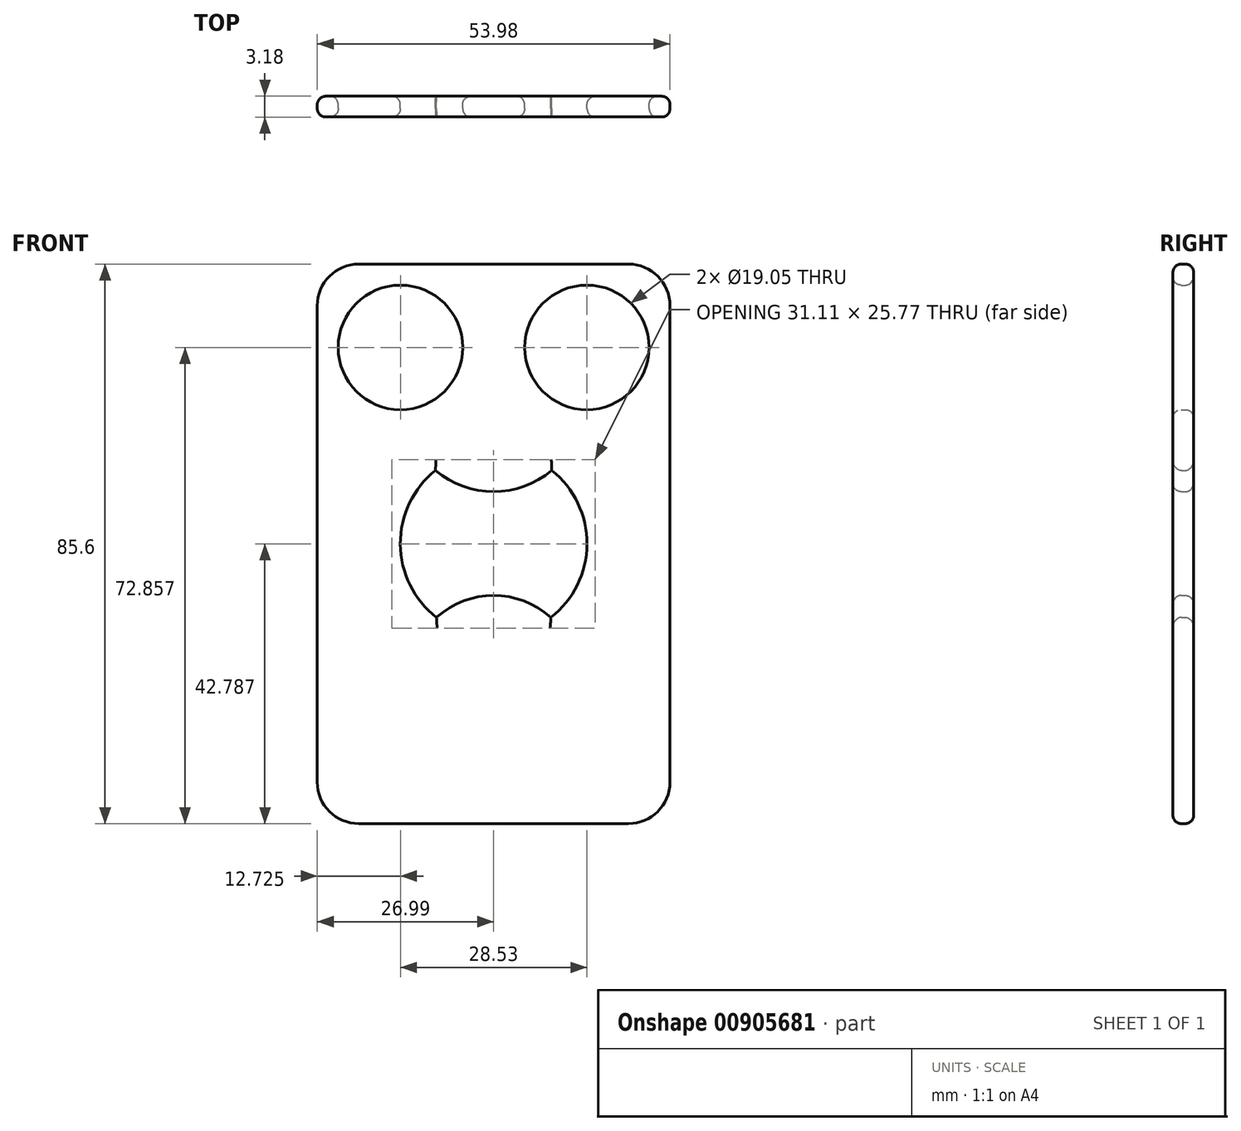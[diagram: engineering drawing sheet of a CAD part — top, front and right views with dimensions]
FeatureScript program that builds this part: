
annotation { "Feature Type Name" : "Feature", "Feature Type Description" : "" }
export const myFeature = defineFeature(function(context is Context, id is Id, definition is map)
    precondition{}
    {
        {
            var Q0;
            Q0=qCreatedBy(makeId("Front.planeOp"),FACE);
            var sketch = newSketch(context, id + "F0", { "sketchPlane" : qUnion([Q0])});
            skLineSegment(sketch, "E0.bottom", {"start": v(-20.64, 42.8) * mm, "end": v(20.64, 42.8) * mm});
            skLineSegment(sketch, "E0.top", {"start": v(-20.64, -42.8) * mm, "end": v(20.64, -42.8) * mm});
            skLineSegment(sketch, "E0.left", {"start": v(-26.99, 36.45) * mm, "end": v(-26.99, -36.45) * mm});
            skLineSegment(sketch, "E0.right", {"start": v(26.99, 36.45) * mm, "end": v(26.99, -36.45) * mm});
            skPoint(sketch, "E0.middle", {"position": v(0, 0) * mm});
            skPoint(sketch, "E1.visualSharp", {"position": v(-26.99, 42.8) * mm});
            skArc(sketch, "E1.filletArc", {"start": v(-20.64, 42.8) * mm, "mid": v(-25.13, 40.94) * mm, "end": v(-26.99, 36.45) * mm});
            skPoint(sketch, "E2.visualSharp", {"position": v(26.99, 42.8) * mm});
            skArc(sketch, "E2.filletArc", {"start": v(26.99, 36.45) * mm, "mid": v(25.13, 40.94) * mm, "end": v(20.64, 42.8) * mm});
            skPoint(sketch, "E3.visualSharp", {"position": v(26.99, -42.8) * mm});
            skArc(sketch, "E3.filletArc", {"start": v(20.64, -42.8) * mm, "mid": v(25.13, -40.94) * mm, "end": v(26.99, -36.45) * mm});
            skPoint(sketch, "E4.visualSharp", {"position": v(-26.99, -42.8) * mm});
            skArc(sketch, "E4.filletArc", {"start": v(-26.99, -36.45) * mm, "mid": v(-25.13, -40.94) * mm, "end": v(-20.64, -42.8) * mm});
            skCircle(sketch, "E5", {"center": v(-14.27, 30.06) * mm, "radius": 9.53 * mm});
            skCircle(sketch, "E6.MirrorC", {"center": v(14.27, 30.06) * mm, "radius": 9.53 * mm});
            skArc(sketch, "E7", {"start": v(-8.9, 11.23) * mm, "mid": v(-14.29, -0.04) * mm, "end": v(-8.75, -11.24) * mm});
            skArc(sketch, "E8", {"start": v(-8.9, 11.23) * mm, "mid": v(0, 7.99) * mm, "end": v(8.9, 11.23) * mm});
            skArc(sketch, "E9", {"start": v(8.75, -11.24) * mm, "mid": v(0, -7.89) * mm, "end": v(-8.75, -11.24) * mm});
            skArc(sketch, "E10.trimOffspring", {"start": v(8.75, -11.24) * mm, "mid": v(14.29, -0.04) * mm, "end": v(8.9, 11.23) * mm});
            skSolve(sketch);
        }
        {
            var Q0;
            Q0=makeQuery(id+"F0.imprint","IMPRINT",FACE,{"disambiguationData":[TD([[makeQuery(id+"F0.imprint","IMPRINT",EDGE,{"derivedFrom":sQuery(id+"F0.wireOp",EDGE,"E0.bottom")}),-1.0]])]});
            extrude(context, id + "F1", {"entities" : qUnion([Q0]), "depth" : 3.17 * mm, "offsetDistance" : 25.4 * mm});
        }
        {
            var Q0;
            Q0=makeQuery(id+"F1.opExtrude","CAP_EDGE",EDGE,{"disambiguationData":[OSD([sQuery(id+"F0.wireOp",EDGE,"E0.left")])],"isStart":false});
            var Q1;
            Q1=makeQuery(id+"F1.opExtrude","CAP_EDGE",EDGE,{"disambiguationData":[OSD([sQuery(id+"F0.wireOp",EDGE,"E5")])],"isStart":false});
            var Q2;
            Q2=makeQuery(id+"F1.opExtrude","CAP_EDGE",EDGE,{"disambiguationData":[OSD([sQuery(id+"F0.wireOp",EDGE,"E6.MirrorC")])],"isStart":false});
            var Q3;
            Q3=makeQuery(id+"F1.opExtrude","CAP_EDGE",EDGE,{"disambiguationData":[OSD([sQuery(id+"F0.wireOp",EDGE,"E8")])],"isStart":false});
            var Q4;
            Q4=makeQuery(id+"F1.opExtrude","CAP_EDGE",EDGE,{"disambiguationData":[OSD([sQuery(id+"F0.wireOp",EDGE,"E10.trimOffspring")])],"isStart":false});
            var Q5;
            Q5=makeQuery(id+"F1.opExtrude","CAP_EDGE",EDGE,{"disambiguationData":[OSD([sQuery(id+"F0.wireOp",EDGE,"E9")])],"isStart":false});
            var Q6;
            Q6=makeQuery(id+"F1.opExtrude","CAP_EDGE",EDGE,{"disambiguationData":[OSD([sQuery(id+"F0.wireOp",EDGE,"E7")])],"isStart":false});
            var Q7;
            Q7=makeQuery(id+"F1.opExtrude","CAP_EDGE",EDGE,{"disambiguationData":[OSD([sQuery(id+"F0.wireOp",EDGE,"E0.right")])],"isStart":true});
            var Q8;
            Q8=makeQuery(id+"F1.opExtrude","CAP_EDGE",EDGE,{"disambiguationData":[OSD([sQuery(id+"F0.wireOp",EDGE,"E6.MirrorC")])],"isStart":true});
            var Q9;
            Q9=makeQuery(id+"F1.opExtrude","CAP_EDGE",EDGE,{"disambiguationData":[OSD([sQuery(id+"F0.wireOp",EDGE,"E5")])],"isStart":true});
            var Q10;
            Q10=makeQuery(id+"F1.opExtrude","CAP_EDGE",EDGE,{"disambiguationData":[OSD([sQuery(id+"F0.wireOp",EDGE,"E7")])],"isStart":true});
            var Q11;
            Q11=makeQuery(id+"F1.opExtrude","CAP_EDGE",EDGE,{"disambiguationData":[OSD([sQuery(id+"F0.wireOp",EDGE,"E9")])],"isStart":true});
            var Q12;
            Q12=makeQuery(id+"F1.opExtrude","CAP_EDGE",EDGE,{"disambiguationData":[OSD([sQuery(id+"F0.wireOp",EDGE,"E10.trimOffspring")])],"isStart":true});
            var Q13;
            Q13=makeQuery(id+"F1.opExtrude","CAP_EDGE",EDGE,{"disambiguationData":[OSD([sQuery(id+"F0.wireOp",EDGE,"E8")])],"isStart":true});
            fillet(context, id + "F2", {"entities" : qUnion([Q0, Q1, Q2, Q3, Q4, Q5, Q6, Q7, Q8, Q9, Q10, Q11, Q12, Q13]), "radius" : 1.27 * mm, "tangentPropagation" : true, "allowEdgeOverflow" : false});
        }
    });
